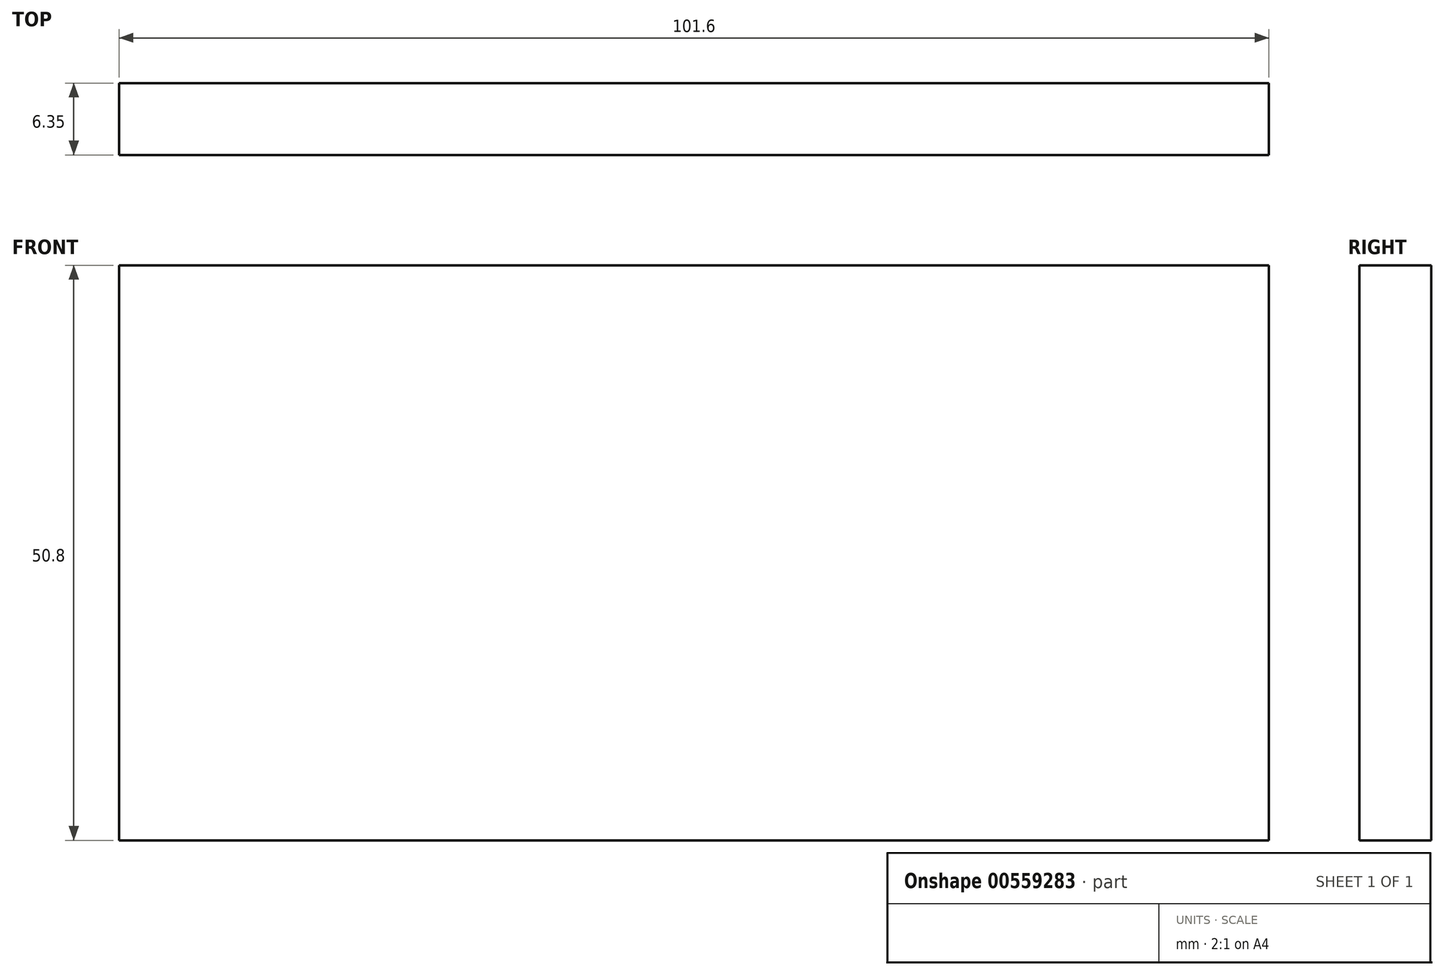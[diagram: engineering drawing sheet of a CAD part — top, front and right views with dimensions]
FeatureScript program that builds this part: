
annotation { "Feature Type Name" : "Feature", "Feature Type Description" : "" }
export const myFeature = defineFeature(function(context is Context, id is Id, definition is map)
    precondition{}
    {
        {
            var Q0;
            Q0=qCreatedBy(makeId("Front.planeOp"),FACE);
            var sketch = newSketch(context, id + "F0", { "sketchPlane" : qUnion([Q0])});
            skLineSegment(sketch, "E0", {"start": v(-50.8, 70.3) * mm, "end": v(-50.8, 19.5) * mm});
            skLineSegment(sketch, "E1", {"start": v(-50.8, 19.5) * mm, "end": v(0, 19.5) * mm});
            skLineSegment(sketch, "E2", {"start": v(0, 19.5) * mm, "end": v(0, 70.3) * mm});
            skLineSegment(sketch, "E3", {"start": v(0, 70.3) * mm, "end": v(-50.8, 70.3) * mm});
            skLineSegment(sketch, "E4", {"start": v(-50.8, 70.3) * mm, "end": v(-25.4, 70.3) * mm});
            skLineSegment(sketch, "E5", {"start": v(-25.4, 19.5) * mm, "end": v(-25.4, 70.3) * mm});
            skLineSegment(sketch, "E6", {"start": v(0, 70.3) * mm, "end": v(50.8, 70.3) * mm});
            skLineSegment(sketch, "E7", {"start": v(50.8, 70.3) * mm, "end": v(50.8, 19.5) * mm});
            skLineSegment(sketch, "E8", {"start": v(50.8, 19.5) * mm, "end": v(0, 19.5) * mm});
            skLineSegment(sketch, "E9", {"start": v(25.4, 70.3) * mm, "end": v(25.4, 19.5) * mm});
            skLineSegment(sketch, "E10", {"start": v(25.4, 19.5) * mm, "end": v(25.4, 70.3) * mm});
            skSolve(sketch);
        }
        {
            var Q0;
            Q0 = qSketchRegion(id + "F0", true);
            extrude(context, id + "F1", {"entities" : qUnion([Q0]), "depth" : 6.35 * mm, "offsetDistance" : 25.4 * mm});
        }
    });
